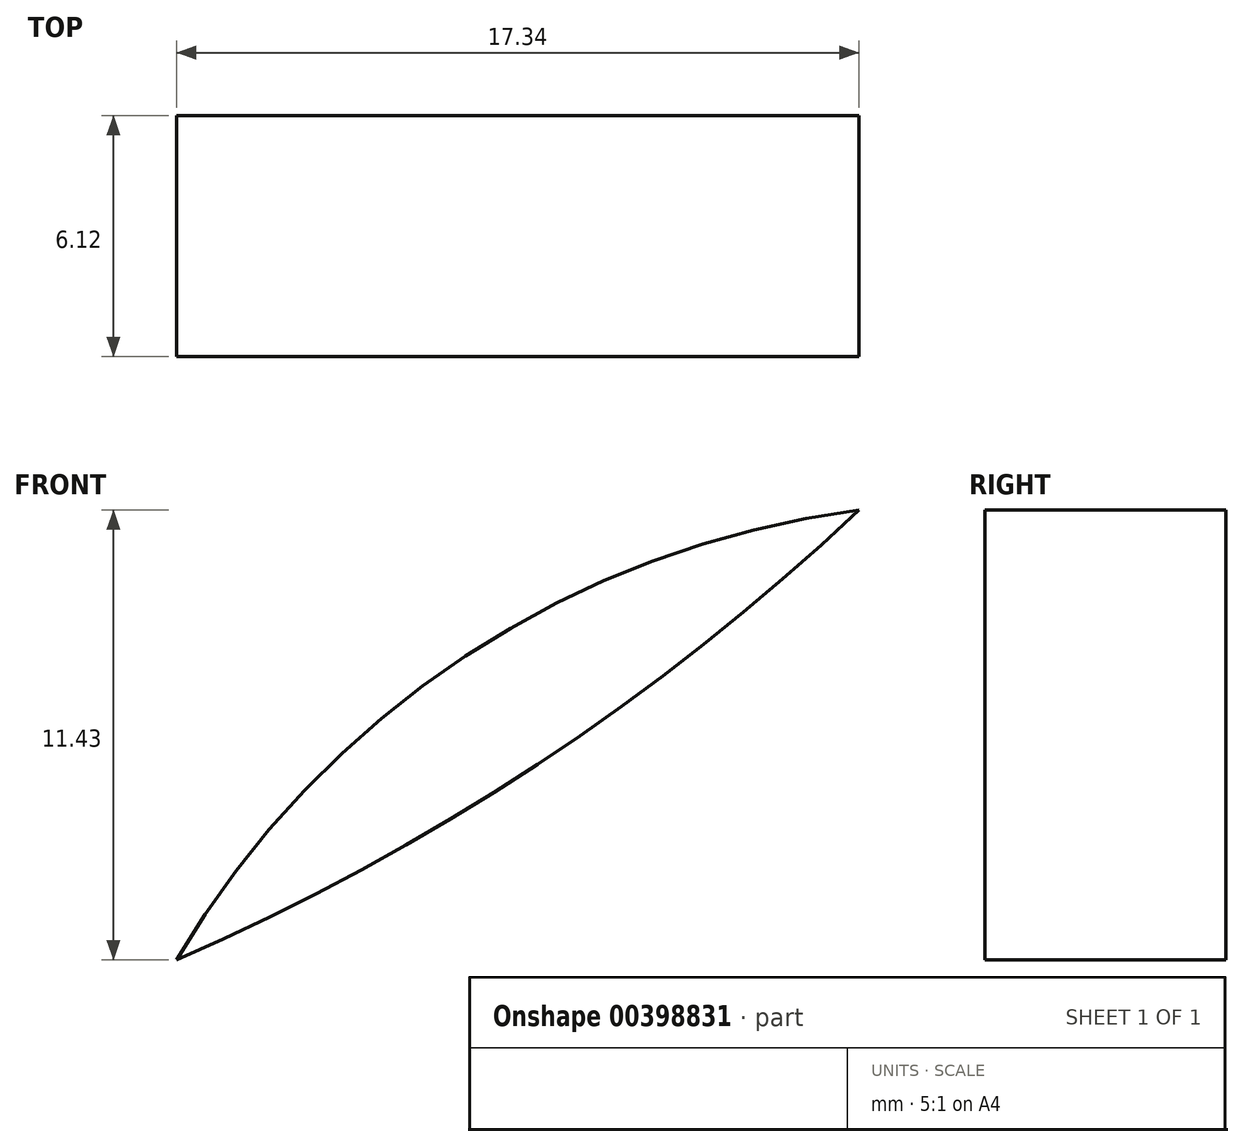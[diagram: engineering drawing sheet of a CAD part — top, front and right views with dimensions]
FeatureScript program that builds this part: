
annotation { "Feature Type Name" : "Feature", "Feature Type Description" : "" }
export const myFeature = defineFeature(function(context is Context, id is Id, definition is map)
    precondition{}
    {
        {
            var Q0;
            Q0=qCreatedBy(makeId("Front.planeOp"),FACE);
            var sketch = newSketch(context, id + "F0", { "sketchPlane" : qUnion([Q0])});
            skArc(sketch, "E0", {"start": v(10.45, 23.4) * mm, "mid": v(0.46, 19.7) * mm, "end": v(-6.89, 11.97) * mm});
            skArc(sketch, "E1", {"start": v(-6.89, 11.97) * mm, "mid": v(2.28, 16.93) * mm, "end": v(10.45, 23.4) * mm});
            skSolve(sketch);
        }
        {
            var Q0;
            Q0 = qSketchRegion(id + "F0", true);
            extrude(context, id + "F1", {"entities" : qUnion([Q0]), "depth" : 6.12 * mm});
        }
    });
